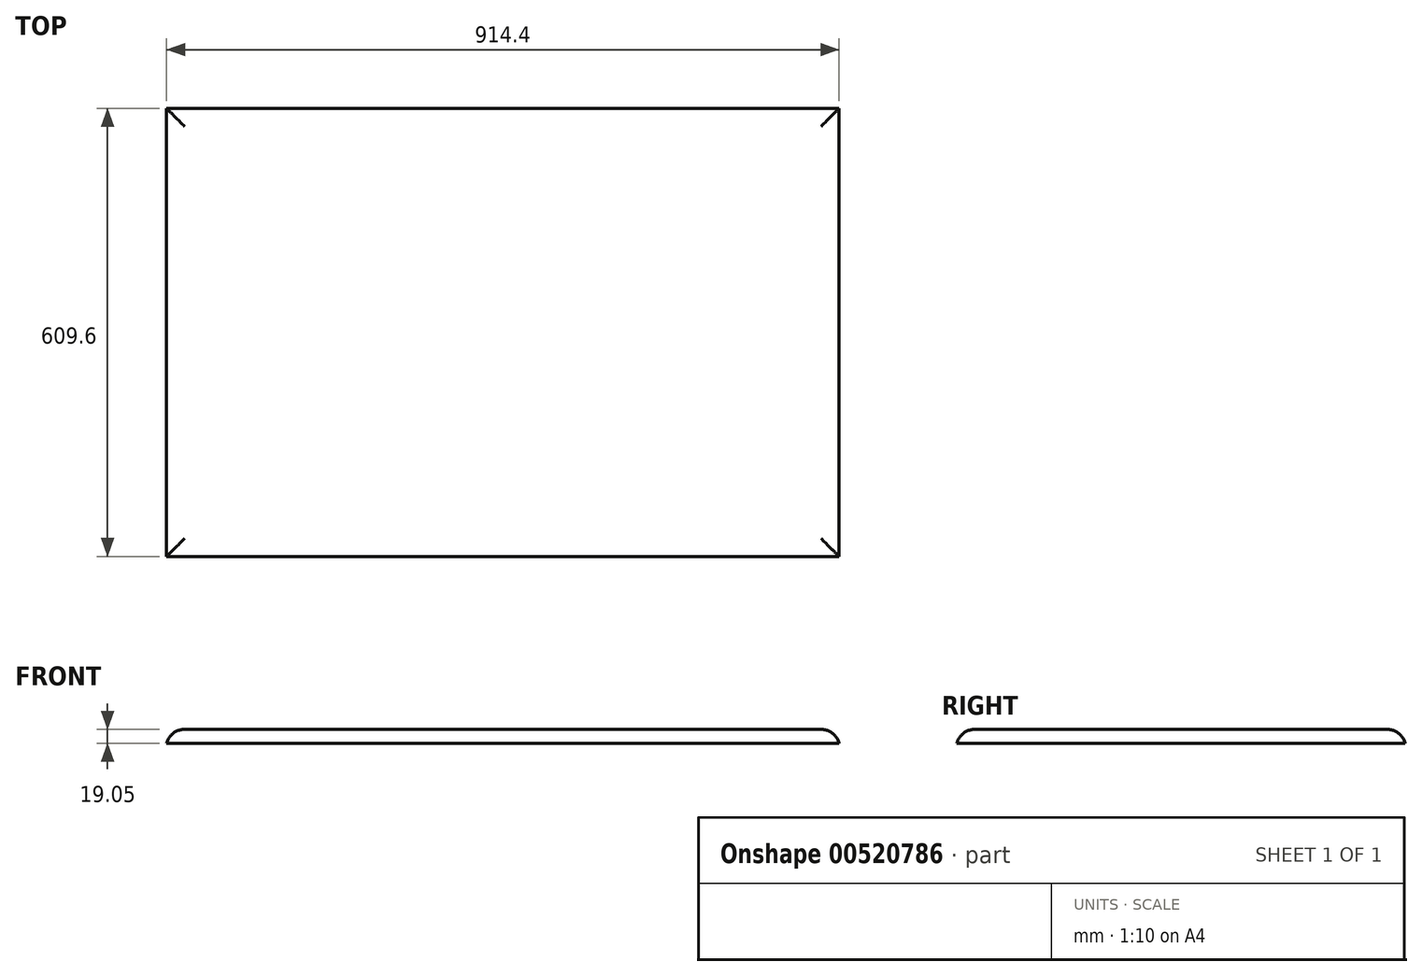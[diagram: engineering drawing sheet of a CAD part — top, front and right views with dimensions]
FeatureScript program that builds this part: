
annotation { "Feature Type Name" : "Feature", "Feature Type Description" : "" }
export const myFeature = defineFeature(function(context is Context, id is Id, definition is map)
    precondition{}
    {
        {
            var Q0;
            Q0=qCreatedBy(makeId("Top.planeOp"),FACE);
            var sketch = newSketch(context, id + "F0", { "sketchPlane" : qUnion([Q0])});
            skLineSegment(sketch, "E0.bottom", {"start": v(0, -162.18) * mm, "end": v(-914.4, -162.18) * mm});
            skLineSegment(sketch, "E0.top", {"start": v(0, 447.42) * mm, "end": v(-914.4, 447.42) * mm});
            skLineSegment(sketch, "E0.left", {"start": v(0, -162.18) * mm, "end": v(0, 447.42) * mm});
            skLineSegment(sketch, "E0.right", {"start": v(-914.4, -162.18) * mm, "end": v(-914.4, 447.42) * mm});
            skSolve(sketch);
        }
        {
            var Q0;
            Q0 = qSketchRegion(id + "F0", true);
            extrude(context, id + "F1", {"entities" : qUnion([Q0]), "depth" : 19.05 * mm, "offsetDistance" : 25.4 * mm});
        }
        {
            var Q0;
            Q0=makeQuery(id+"F1.opExtrude","CAP_EDGE",EDGE,{"disambiguationData":[OSD([sQuery(id+"F0.wireOp",EDGE,"E0.left")])],"isStart":false});
            var Q1;
            Q1=makeQuery(id+"F1.opExtrude","CAP_FACE",FACE,{"disambiguationData":[OSD([sQuery(id+"F0.wireOp",EDGE,"E0.bottom"),sQuery(id+"F0.wireOp",EDGE,"E0.top"),sQuery(id+"F0.wireOp",EDGE,"E0.left"),sQuery(id+"F0.wireOp",EDGE,"E0.right")])],"isStart":false});
            fillet(context, id + "F2", {"entities" : qUnion([Q0, Q1]), "radius" : 25.4 * mm, "tangentPropagation" : true, "allowEdgeOverflow" : false});
        }
    });
